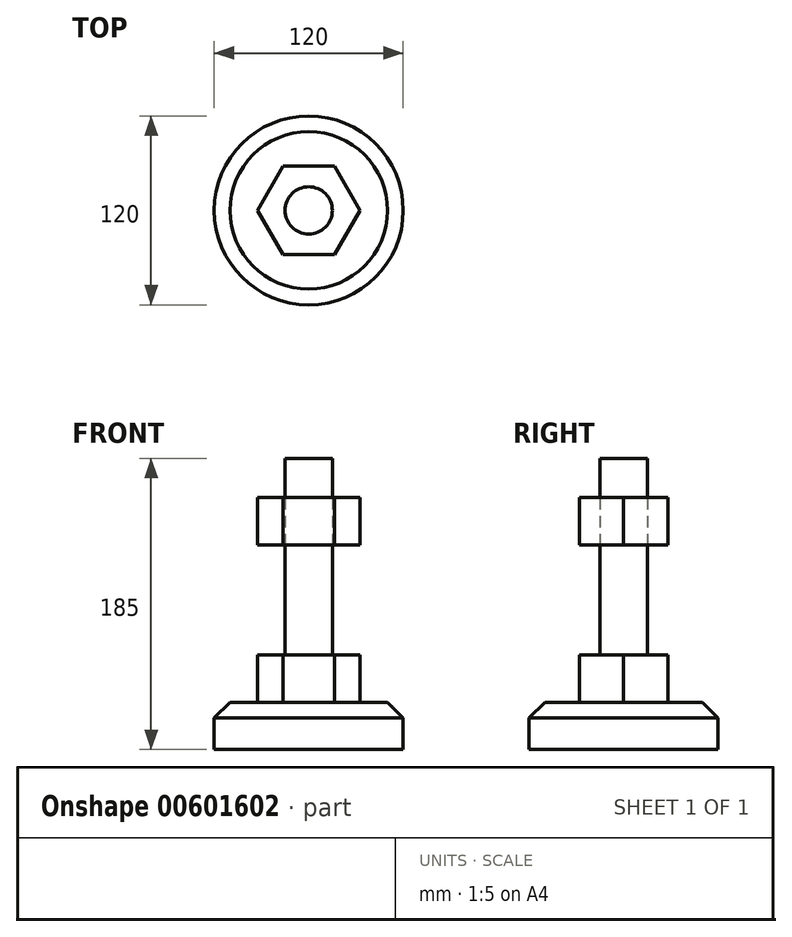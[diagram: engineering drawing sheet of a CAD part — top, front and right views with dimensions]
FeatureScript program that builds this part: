
annotation { "Feature Type Name" : "Feature", "Feature Type Description" : "" }
export const myFeature = defineFeature(function(context is Context, id is Id, definition is map)
    precondition{}
    {
        {
            var Q0;
            Q0=qCreatedBy(makeId("Top.planeOp"),FACE);
            var sketch = newSketch(context, id + "F0", { "sketchPlane" : qUnion([Q0])});
            skCircle(sketch, "E0", {"center": v(0, 0) * mm, "radius": 60 * mm});
            skSolve(sketch);
        }
        {
            var Q0;
            Q0=makeQuery(id+"F0.imprint","IMPRINT",FACE,{"disambiguationData":[TD([[makeQuery(id+"F0.imprint","IMPRINT",EDGE,{"derivedFrom":sQuery(id+"F0.wireOp",EDGE,"E0")}),1.0]])]});
            extrude(context, id + "F1", {"entities" : qUnion([Q0]), "depth" : 30 * mm, "offsetDistance" : 25 * mm});
        }
        {
            var Q0;
            Q0=makeQuery(id+"F1.opExtrude","CAP_EDGE",EDGE,{"disambiguationData":[OSD([sQuery(id+"F0.wireOp",EDGE,"E0")])],"isStart":false});
            chamfer(context, id + "F2", {"entities" : qUnion([Q0]), "width" : 10 * mm, "tangentPropagation" : true});
        }
        {
            var Q0;
            Q0=makeQuery(id+"F1.opExtrude","CAP_FACE",FACE,{"disambiguationData":[OSD([sQuery(id+"F0.wireOp",EDGE,"E0")])],"isStart":false});
            var sketch = newSketch(context, id + "F3", { "sketchPlane" : qUnion([Q0])});
            skCircle(sketch, "E1.cCircle", {"center": v(0, 0) * mm, "radius": 28.15 * mm, "construction": true});
            skLineSegment(sketch, "E1.0", {"start": v(16.25, 28.15) * mm, "end": v(32.5, 0) * mm});
            skLineSegment(sketch, "E1.1", {"start": v(32.5, 0) * mm, "end": v(16.25, -28.15) * mm});
            skLineSegment(sketch, "E1.2", {"start": v(16.25, -28.15) * mm, "end": v(-16.25, -28.15) * mm});
            skLineSegment(sketch, "E1.3", {"start": v(-16.25, -28.15) * mm, "end": v(-32.5, 0) * mm});
            skLineSegment(sketch, "E1.4", {"start": v(-32.5, 0) * mm, "end": v(-16.25, 28.15) * mm});
            skLineSegment(sketch, "E1.5", {"start": v(-16.25, 28.15) * mm, "end": v(16.25, 28.15) * mm});
            skPoint(sketch, "E1.0.midPoint", {"position": v(24.38, 14.07) * mm});
            skSolve(sketch);
        }
        {
            var Q0;
            Q0=makeQuery(id+"F3.imprint","IMPRINT",FACE,{"disambiguationData":[TD([[makeQuery(id+"F3.imprint","IMPRINT",EDGE,{"derivedFrom":sQuery(id+"F3.wireOp",EDGE,"E1.0")}),-1.0]])]});
            extrude(context, id + "F4", {"entities" : qUnion([Q0]), "operationType" : NewBodyOperationType.ADD, "depth" : 30 * mm, "offsetDistance" : 25 * mm});
        }
        {
            var Q0;
            Q0=makeQuery(id+"F4.opExtrude","CAP_FACE",FACE,{"disambiguationData":[OSD([sQuery(id+"F3.wireOp",EDGE,"E1.0"),sQuery(id+"F3.wireOp",EDGE,"E1.1"),sQuery(id+"F3.wireOp",EDGE,"E1.2"),sQuery(id+"F3.wireOp",EDGE,"E1.3"),sQuery(id+"F3.wireOp",EDGE,"E1.4"),sQuery(id+"F3.wireOp",EDGE,"E1.5")])],"isStart":false});
            extrude(context, id + "F5", {"entities" : qUnion([Q0]), "depth" : 30 * mm, "offsetDistance" : 25 * mm});
        }
        {
            var Q0;
            Q0=makeQuery(id+"F5.opExtrude","SWEPT_BODY",BODY,{"disambiguationData":[OSD([sQuery(id+"F3.wireOp",EDGE,"E1.0"),sQuery(id+"F3.wireOp",EDGE,"E1.1"),sQuery(id+"F3.wireOp",EDGE,"E1.2"),sQuery(id+"F3.wireOp",EDGE,"E1.3"),sQuery(id+"F3.wireOp",EDGE,"E1.4"),sQuery(id+"F3.wireOp",EDGE,"E1.5")])]});
            transform(context, id + "F6", {"entities" : qUnion([Q0]), "transformType" : TransformType.TRANSLATION_3D, "dx" : 0 * mm, "dy" : 0 * mm, "dz" : 95 * mm, "makeCopy" : false});
        }
        {
            var Q0;
            Q0=makeQuery(id+"F4.opExtrude","CAP_FACE",FACE,{"disambiguationData":[OSD([sQuery(id+"F3.wireOp",EDGE,"E1.0"),sQuery(id+"F3.wireOp",EDGE,"E1.1"),sQuery(id+"F3.wireOp",EDGE,"E1.2"),sQuery(id+"F3.wireOp",EDGE,"E1.3"),sQuery(id+"F3.wireOp",EDGE,"E1.4"),sQuery(id+"F3.wireOp",EDGE,"E1.5")])],"isStart":false});
            var sketch = newSketch(context, id + "F7", { "sketchPlane" : qUnion([Q0])});
            skCircle(sketch, "E2", {"center": v(0, 0) * mm, "radius": 15 * mm});
            skSolve(sketch);
        }
        {
            var Q0;
            Q0=makeQuery(id+"F7.imprint","IMPRINT",FACE,{"disambiguationData":[TD([[makeQuery(id+"F7.imprint","IMPRINT",EDGE,{"derivedFrom":sQuery(id+"F7.wireOp",EDGE,"E2")}),1.0]])]});
            extrude(context, id + "F8", {"entities" : qUnion([Q0]), "depth" : 125 * mm, "offsetDistance" : 25 * mm});
        }
        {
            var Q0;
            Q0=makeQuery(id+"F5.opExtrude","SWEPT_BODY",BODY,{"disambiguationData":[OSD([sQuery(id+"F3.wireOp",EDGE,"E1.0"),sQuery(id+"F3.wireOp",EDGE,"E1.1"),sQuery(id+"F3.wireOp",EDGE,"E1.2"),sQuery(id+"F3.wireOp",EDGE,"E1.3"),sQuery(id+"F3.wireOp",EDGE,"E1.4"),sQuery(id+"F3.wireOp",EDGE,"E1.5")])]});
            transform(context, id + "F9", {"entities" : qUnion([Q0]), "transformType" : TransformType.TRANSLATION_3D, "dx" : 0 * mm, "dy" : 0 * mm, "dz" : -25 * mm, "makeCopy" : false});
        }
    });
